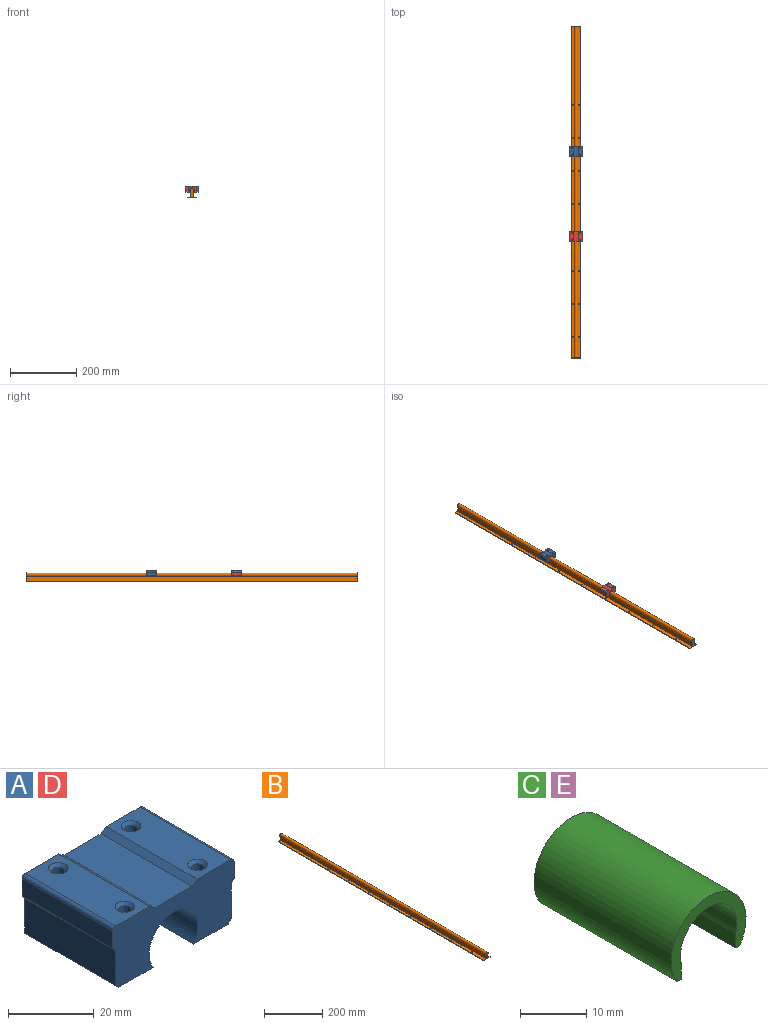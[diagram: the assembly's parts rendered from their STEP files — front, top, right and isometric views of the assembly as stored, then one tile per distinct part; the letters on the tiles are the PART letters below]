
ASSEMBLY  parts=5 mates=4
PART A: 28 faces, bbox 40x30x18 mm
  f0: plane 30x11.43mm, normal (0,0,-1), area 328.9mm2, adj f1,f2,f3,f4,f23,f25
  f1: plane 40x18mm, normal (0,-1,0), area 514.1mm2, adj f0,f7,f8,f9,f10,f11,f12,f13
  f2: plane 40x18mm, normal (0,1,0), area 514.1mm2, adj f0,f7,f8,f9,f10,f11,f12,f13
  f3: cylinder r=1.5mm len=17.2mm, axis (0,0,1), area 162.1mm2, adj f0,f20
  f4: cylinder r=1.5mm len=17.2mm, axis (0,0,1), area 162.1mm2, adj f0,f19
  f5: cylinder r=1.5mm len=17.2mm, axis (0,0,1), area 162.1mm2, adj f15,f21
  f6: cylinder r=1.5mm len=17.2mm, axis (0,0,1), area 162.1mm2, adj f15,f22
  f7: plane 30x11.19mm, normal (0,0,1), area 302.3mm2, adj f1,f2,f8,f19,f20,f27
  f8: plane 30x1.71mm, normal (-0.57,0,0.82), area 62.8mm2, adj f1,f2,f7,f9
  f9: plane 30x12.2mm, normal (0,0,1), area 366mm2, adj f1,f2,f8,f10
  f10: plane 30x1.71mm, normal (0.57,0,0.82), area 62.8mm2, adj f1,f2,f9,f11
  f11: plane 30x11.19mm, normal (0,0,1), area 302.3mm2, adj f1,f2,f10,f21,f22,f26
  f12: plane 30x5mm, normal (-1,0,0), area 150mm2, adj f1,f2,f13,f26
  f13: plane 30x1mm, normal (-0.75,0,-0.66), area 40.2mm2, adj f1,f2,f12,f14
  f14: plane 30x10mm, normal (-1,0,0), area 300mm2, adj f1,f2,f13,f24
  f15: plane 30x11.43mm, normal (0,0,-1), area 328.9mm2, adj f1,f2,f5,f6,f23,f24
  f16: plane 30x10mm, normal (1,0,0), area 300mm2, adj f1,f2,f17,f25
  f17: plane 30x1mm, normal (0.75,0,-0.66), area 40.2mm2, adj f1,f2,f16,f18
  f18: plane 30x5mm, normal (1,0,0), area 150mm2, adj f1,f2,f17,f27
  f19: cone r=1.5mm half-angle=45deg, axis (0,0,1), area 13.5mm2, adj f4,f7
  f20: cone r=1.5mm half-angle=45deg, axis (0,0,1), area 13.5mm2, adj f3,f7
  f21: cone r=1.5mm half-angle=45deg, axis (0,0,1), area 13.5mm2, adj f5,f11
  f22: cone r=1.5mm half-angle=45deg, axis (0,0,1), area 13.5mm2, adj f6,f11
  f23: cylinder r=8mm len=30mm, axis (0,-1,0), area 1034.1mm2, adj f0,f1,f2,f15
  f24: plane 30x1mm, normal (-0.71,0,-0.71), area 42.4mm2, adj f1,f2,f14,f15
  f25: plane 30x1mm, normal (0.71,0,-0.71), area 42.4mm2, adj f0,f1,f2,f16
  f26: cylinder r=1mm len=30mm, axis (0,-1,0), area 47.1mm2, adj f1,f2,f11,f12
  f27: cylinder r=1mm len=30mm, axis (0,1,0), area 47.1mm2, adj f1,f2,f7,f18
PART B: 26 faces, bbox 30x1000x28 mm
  f0: cylinder r=1.5mm len=3mm, axis (0,0,1), area 18.8mm2, adj f14,f20
  f1: cylinder r=1.5mm len=3mm, axis (0,0,1), area 18.8mm2, adj f14,f20
  f2: cylinder r=1.5mm len=3mm, axis (0,0,1), area 18.8mm2, adj f14,f20
  f3: cylinder r=1.5mm len=3mm, axis (0,0,1), area 18.8mm2, adj f14,f20
  f4: cylinder r=1.5mm len=3mm, axis (0,0,1), area 18.8mm2, adj f14,f20
  f5: cylinder r=1.5mm len=3mm, axis (0,0,1), area 18.8mm2, adj f14,f20
  f6: cylinder r=1.5mm len=3mm, axis (0,0,1), area 18.8mm2, adj f14,f20
  f7: cylinder r=1.5mm len=3mm, axis (0,0,1), area 18.8mm2, adj f14,f16
  f8: cylinder r=1.5mm len=3mm, axis (0,0,1), area 18.8mm2, adj f14,f16
  f9: cylinder r=1.5mm len=3mm, axis (0,0,1), area 18.8mm2, adj f14,f16
  f10: cylinder r=1.5mm len=3mm, axis (0,0,1), area 18.8mm2, adj f14,f16
  f11: cylinder r=1.5mm len=3mm, axis (0,0,1), area 18.8mm2, adj f14,f16
  f12: cylinder r=1.5mm len=3mm, axis (0,0,1), area 18.8mm2, adj f14,f16
  f13: cylinder r=1.5mm len=3mm, axis (0,0,1), area 18.8mm2, adj f14,f16
  f14: plane 1000x30mm, normal (0,0,-1), area 29886.9mm2, adj f0,f1,f2,f3,f4,f5,f6,f7
  f15: plane 1000x2mm, normal (1,0,0), area 2000mm2, adj f14,f16,f22,f23
  f16: plane 1000x11mm, normal (0,0,1), area 10943.5mm2, adj f7,f8,f9,f10,f11,f12,f13,f15
  f17: plane 1000x15.53mm, normal (1,0,0), area 15527.9mm2, adj f16,f18,f22,f23
  f18: cylinder r=6mm len=1000mm, axis (0,1,0), area 28942.4mm2, adj f17,f19,f22,f23
  f19: plane 1000x15.53mm, normal (-1,0,0), area 15527.9mm2, adj f18,f20,f22,f23
  f20: plane 1000x11mm, normal (0,0,1), area 10943.5mm2, adj f0,f1,f2,f3,f4,f5,f6,f19
  f21: plane 1000x2mm, normal (-1,0,0), area 2000mm2, adj f14,f20,f22,f23
  f22: plane 30x28mm, normal (0,-1,0), area 288.9mm2, adj f14,f15,f16,f17,f18,f19,f20,f21
  f23: plane 30x28mm, normal (0,1,0), area 288.9mm2, adj f14,f15,f16,f17,f18,f19,f20,f21
  f24: cylinder r=1.5mm len=3mm, axis (0,0,1), area 18.8mm2, adj f14,f16
  f25: cylinder r=1.5mm len=3mm, axis (0,0,1), area 18.8mm2, adj f14,f20
PART C: 8 faces, bbox 16x29.3x12.4 mm
  f0: cylinder r=6mm len=29.28mm, axis (0,1,0), area 655mm2, adj f2,f3,f6,f7
  f1: cylinder r=8mm len=29.28mm, axis (0,1,0), area 1009.3mm2, adj f2,f3,f4,f5
  f2: plane 16x12.41mm, normal (0,-1,0), area 59.3mm2, adj f0,f1,f4,f5,f6,f7
  f3: plane 16x12.41mm, normal (0,1,0), area 59.3mm2, adj f0,f1,f4,f5,f6,f7
  f4: plane 29.28x0.85mm, normal (0,0,-1), area 24.8mm2, adj f1,f2,f3,f6
  f5: plane 29.28x0.85mm, normal (0,0,-1), area 24.8mm2, adj f1,f2,f3,f7
  f6: plane 29.28x2.67mm, normal (-1,0,-0.03), area 78.3mm2, adj f0,f2,f3,f4
  f7: plane 29.28x2.67mm, normal (1,0,-0.03), area 78.3mm2, adj f0,f2,f3,f5
PART D: same geometry as A
PART E: same geometry as C
PLACE A t=(0,121.27,0)mm
PLACE B at identity fixed
PLACE C t=(0,-134.21,0)mm
PLACE D t=(0,-134.21,0)mm
PLACE E t=(0,121.27,0)mm
MATE fastened C.f0 <-> D.f23  axis (0,1,0) through (0,-134.21,-13.59)mm
MATE slider E.f0 <-> B.f18  axis (0,1,0) through (0,121.27,-13.59)mm
MATE slider C.f0 <-> B.f18  axis (0,1,0) through (0,-134.21,-13.59)mm
MATE fastened E.f0 <-> A.f23  axis (0,1,0) through (0,121.27,-13.59)mm
